# Revit family: Towel_Bar-DXV-Modulus-D35120240_Series
name_source: partatom
category: Specialty Equipment
units: mm (PartAtom-declared; Revit-internal decimal feet)

## family parameters
Cut with Voids When Loaded = No
Host = Face
OmniClass Number = 23.40.20.21.27
OmniClass Title = Towel Bars
Part Type = Normal
Room Calculation Point = No
Round Connector Dimension = Use Diameter
Shared = Yes

## types (4) — shared parameters
Assembly Code = E2010
Default Elevation = 36"
Description = DXV Modulus 24" Towel Bar
Diameter = 1 3/4"
Installation Instruction Link = https://dxv01.blob.core.windows.net
Installation Type = Surface Mounted
Length = 25 9/16"
Manufacturer = DXV
Price = Prices may vary. Please consult Manufacturer Representative for most up-to-date price list.
Product Documentation Link = https://dxv01.blob.core.windows.net
Product Page URL = https://www.dxv.com
Revised Date = 02/24/2022
URL = https://www.dxv.com
Width = 3 13/16"

## per-type parameters (varying)
| type | Finish | Finish 2 | Material |
| D35120240.100 | Brass-DXV-100-Polished Chrome | Brass-DXV-144-Brushed Nickel | Brass-DXV-100-Polished Chrome |
| D35120240.144 | Brass-DXV-144-Brushed Nickel | Brass-DXV-100-Polished Chrome | Brass-DXV-144-Brushed Nickel |
| D35120240.150 | Brass-DXV-150-Platinum Nickel | Brass-DXV-144-Brushed Nickel | Brass-DXV-150-Platinum Nickel |
| D35120240.243 | Brass-DXV-243-Matte Black | Brass-DXV-Black-Polished | Brass-DXV-243-Matte Black |

note: column(s) folded — value = type name in every type: Model

## geometry (parser evidence)
native form markers: Sweep x3
no freeform markers — native parametric forms only
